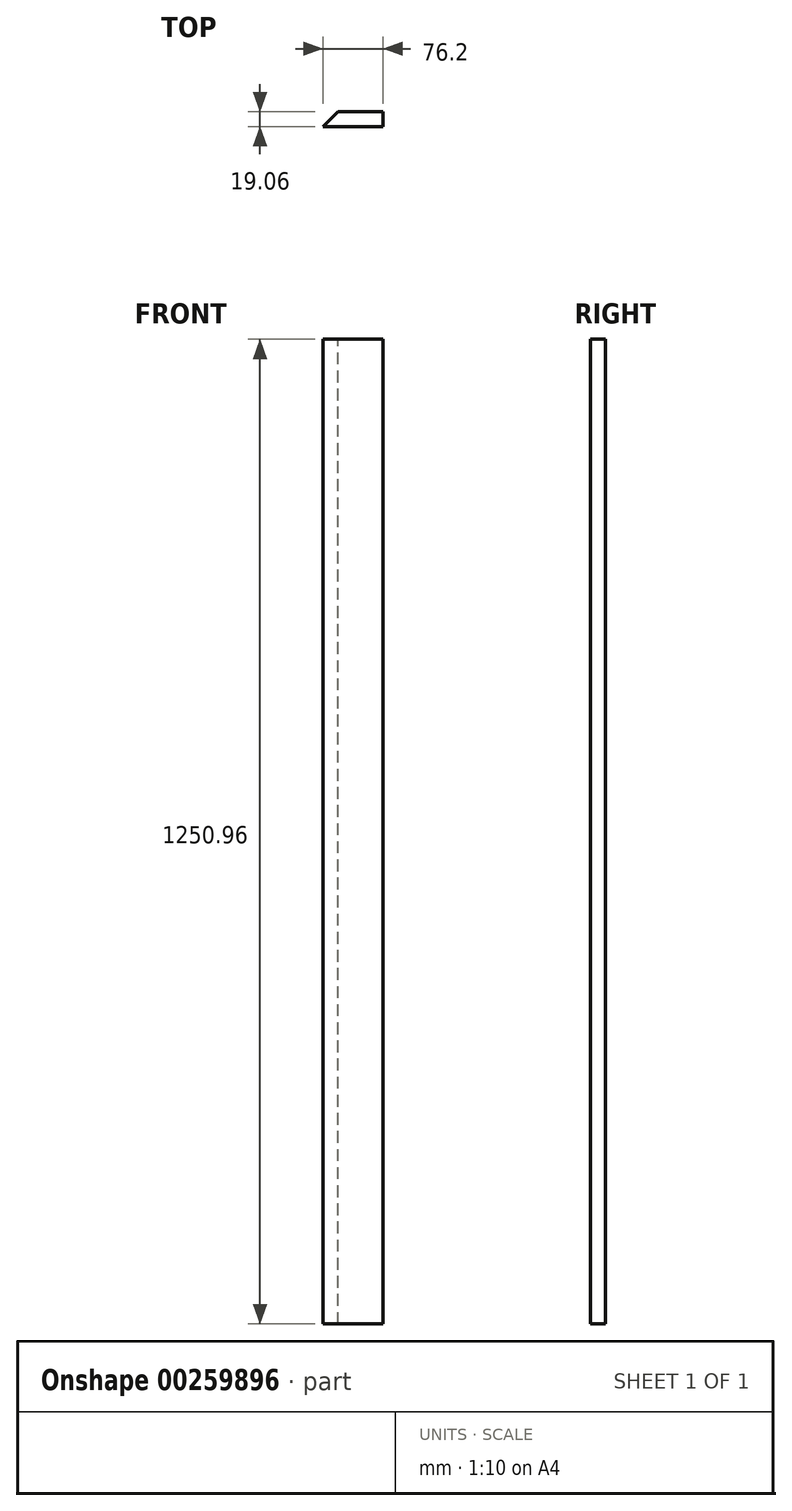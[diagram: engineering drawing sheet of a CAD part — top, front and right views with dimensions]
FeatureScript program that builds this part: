
annotation { "Feature Type Name" : "Feature", "Feature Type Description" : "" }
export const myFeature = defineFeature(function(context is Context, id is Id, definition is map)
    precondition{}
    {
        {
            var Q0;
            Q0=qCreatedBy(makeId("Top.planeOp"),FACE);
            var sketch = newSketch(context, id + "F0", { "sketchPlane" : qUnion([Q0])});
            skLineSegment(sketch, "E0.bottom", {"start": v(-38.1, 9.52) * mm, "end": v(38.1, 9.53) * mm});
            skLineSegment(sketch, "E0.top", {"start": v(-38.1, -9.53) * mm, "end": v(38.1, -9.52) * mm});
            skLineSegment(sketch, "E0.left", {"start": v(-38.1, 9.52) * mm, "end": v(-38.1, -9.53) * mm});
            skLineSegment(sketch, "E0.right", {"start": v(38.1, 9.53) * mm, "end": v(38.1, -9.52) * mm});
            skSolve(sketch);
        }
        {
            var Q0;
            Q0=makeQuery(id+"F0.imprint","IMPRINT",FACE,{"disambiguationData":[TD([[makeQuery(id+"F0.imprint","IMPRINT",EDGE,{"derivedFrom":sQuery(id+"F0.wireOp",EDGE,"E0.bottom")}),-1.0]])]});
            extrude(context, id + "F1", {"entities" : qUnion([Q0]), "endBound" : BoundingType.SYMMETRIC, "depth" : 1250.95 * mm});
        }
        {
            var Q0;
            Q0=makeQuery(id+"F1.opExtrude","SWEPT_EDGE",EDGE,{"disambiguationData":[OSD([sQuery(id+"F0.wireOp",EDGE,"E0.bottom"),sQuery(id+"F0.wireOp",EDGE,"E0.left")])]});
            chamfer(context, id + "F2", {"entities" : qUnion([Q0]), "chamferType" : ChamferType.OFFSET_ANGLE, "width" : 19.05 * mm, "oppositeDirection" : false, "angle" : 45 * degree, "tangentPropagation" : true});
        }
    });
